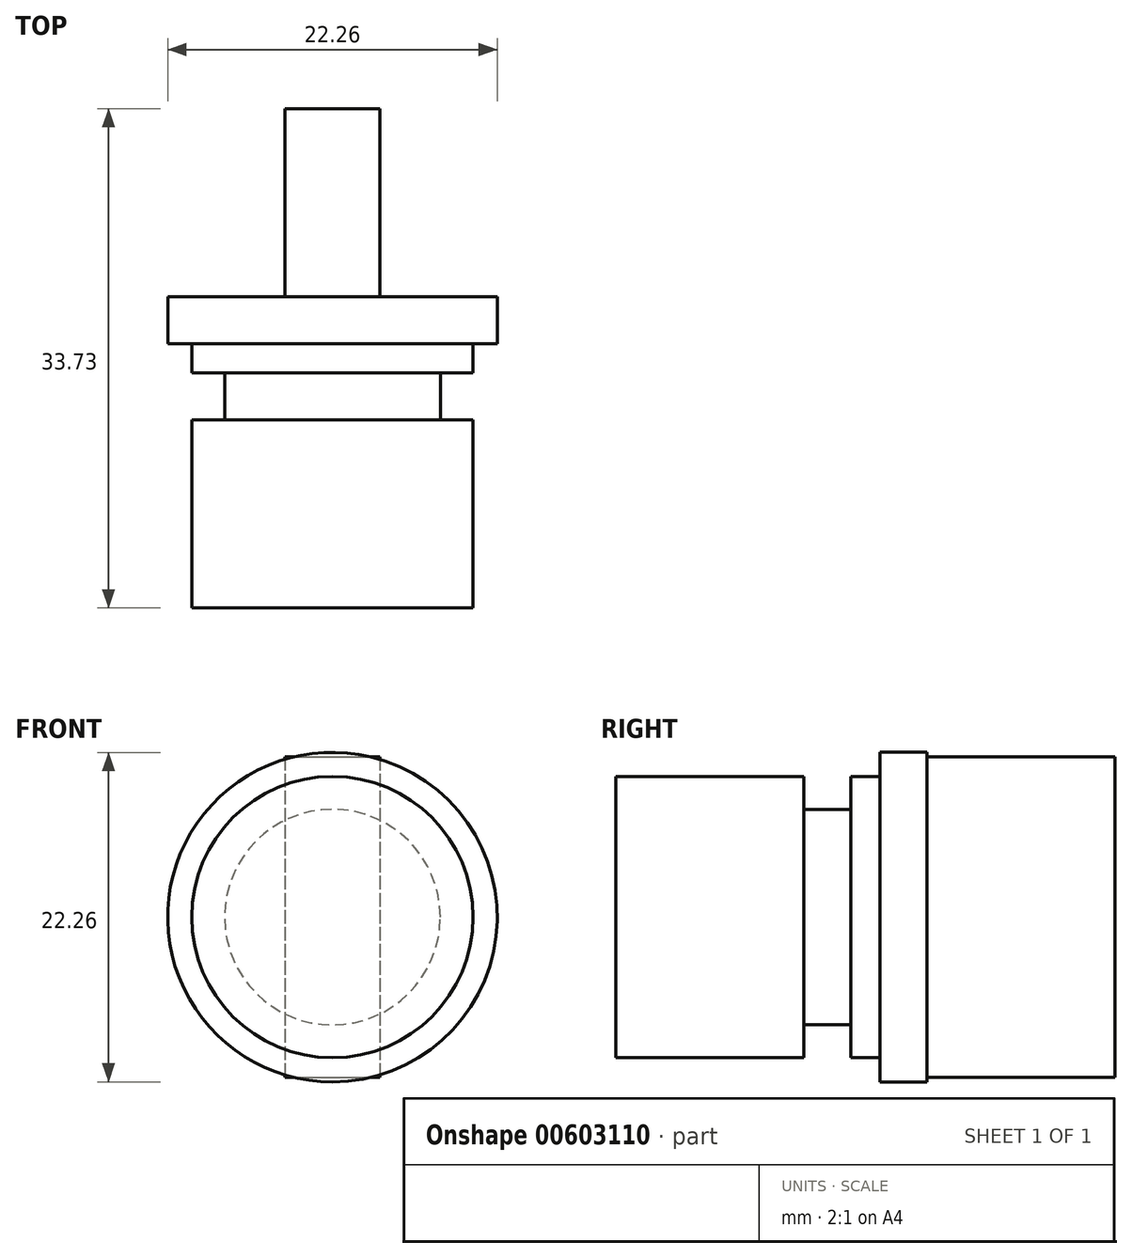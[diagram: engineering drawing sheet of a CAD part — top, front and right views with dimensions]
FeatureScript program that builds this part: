
annotation { "Feature Type Name" : "Feature", "Feature Type Description" : "" }
export const myFeature = defineFeature(function(context is Context, id is Id, definition is map)
    precondition{}
    {
        {
            var Q0;
            Q0=qCreatedBy(makeId("Front.planeOp"),FACE);
            var sketch = newSketch(context, id + "F0", { "sketchPlane" : qUnion([Q0])});
            skCircle(sketch, "E0", {"center": v(0, 0) * mm, "radius": 11.13 * mm});
            skSolve(sketch);
        }
        {
            var Q0;
            Q0=qSketchRegion(id+"F0",true);
            extrude(context, id + "F1", {"entities" : qUnion([Q0]), "depth" : 3.17 * mm, "offsetDistance" : 25.4 * mm});
        }
        {
            var Q0;
            Q0=qCreatedBy(makeId("Front.planeOp"),FACE);
            var sketch = newSketch(context, id + "F2", { "sketchPlane" : qUnion([Q0])});
            skLineSegment(sketch, "E1.bottom", {"start": v(-3.2, 10.83) * mm, "end": v(3.2, 10.83) * mm});
            skLineSegment(sketch, "E1.top", {"start": v(-3.2, -10.83) * mm, "end": v(3.2, -10.83) * mm});
            skLineSegment(sketch, "E1.left", {"start": v(-3.2, 10.83) * mm, "end": v(-3.2, -10.83) * mm});
            skLineSegment(sketch, "E1.right", {"start": v(3.2, 10.83) * mm, "end": v(3.2, -10.83) * mm});
            skPoint(sketch, "E1.middle", {"position": v(0, 0) * mm});
            skSolve(sketch);
        }
        {
            var Q0;
            Q0=qSketchRegion(id+"F2",true);
            extrude(context, id + "F3", {"entities" : qUnion([Q0]), "operationType" : NewBodyOperationType.ADD, "oppositeDirection" : true, "depth" : 12.7 * mm, "offsetDistance" : 25.4 * mm});
        }
        {
            var Q0;
            Q0=qCreatedBy(makeId("Front.planeOp"),FACE);
            var sketch = newSketch(context, id + "F4", { "sketchPlane" : qUnion([Q0])});
            skCircle(sketch, "E2", {"center": v(0, 0) * mm, "radius": 9.48 * mm});
            skSolve(sketch);
        }
        {
            var Q0;
            Q0=qSketchRegion(id+"F4",true);
            extrude(context, id + "F5", {"entities" : qUnion([Q0]), "operationType" : NewBodyOperationType.ADD, "depth" : 5.16 * mm, "offsetDistance" : 25.4 * mm});
        }
        {
            var Q0;
            Q0=qCreatedBy(makeId("Front.planeOp"),FACE);
            var sketch = newSketch(context, id + "F6", { "sketchPlane" : qUnion([Q0])});
            skCircle(sketch, "E3", {"center": v(0, 0) * mm, "radius": 7.28 * mm});
            skSolve(sketch);
        }
        {
            var Q0;
            Q0=qSketchRegion(id+"F6",true);
            extrude(context, id + "F7", {"entities" : qUnion([Q0]), "operationType" : NewBodyOperationType.ADD, "depth" : 8.33 * mm, "offsetDistance" : 25.4 * mm});
        }
        {
            var Q0;
            Q0=makeQuery(id+"F7.opExtrude","CAP_FACE",FACE,{"disambiguationData":[OSD([sQuery(id+"F6.wireOp",EDGE,"E3")])],"isStart":false});
            var sketch = newSketch(context, id + "F8", { "sketchPlane" : qUnion([Q0])});
            skCircle(sketch, "E4", {"center": v(0, 0) * mm, "radius": 9.5 * mm});
            skSolve(sketch);
        }
        {
            var Q0;
            Q0=qSketchRegion(id+"F8",true);
            extrude(context, id + "F9", {"entities" : qUnion([Q0]), "operationType" : NewBodyOperationType.ADD, "depth" : 12.7 * mm, "offsetDistance" : 25.4 * mm});
        }
    });
